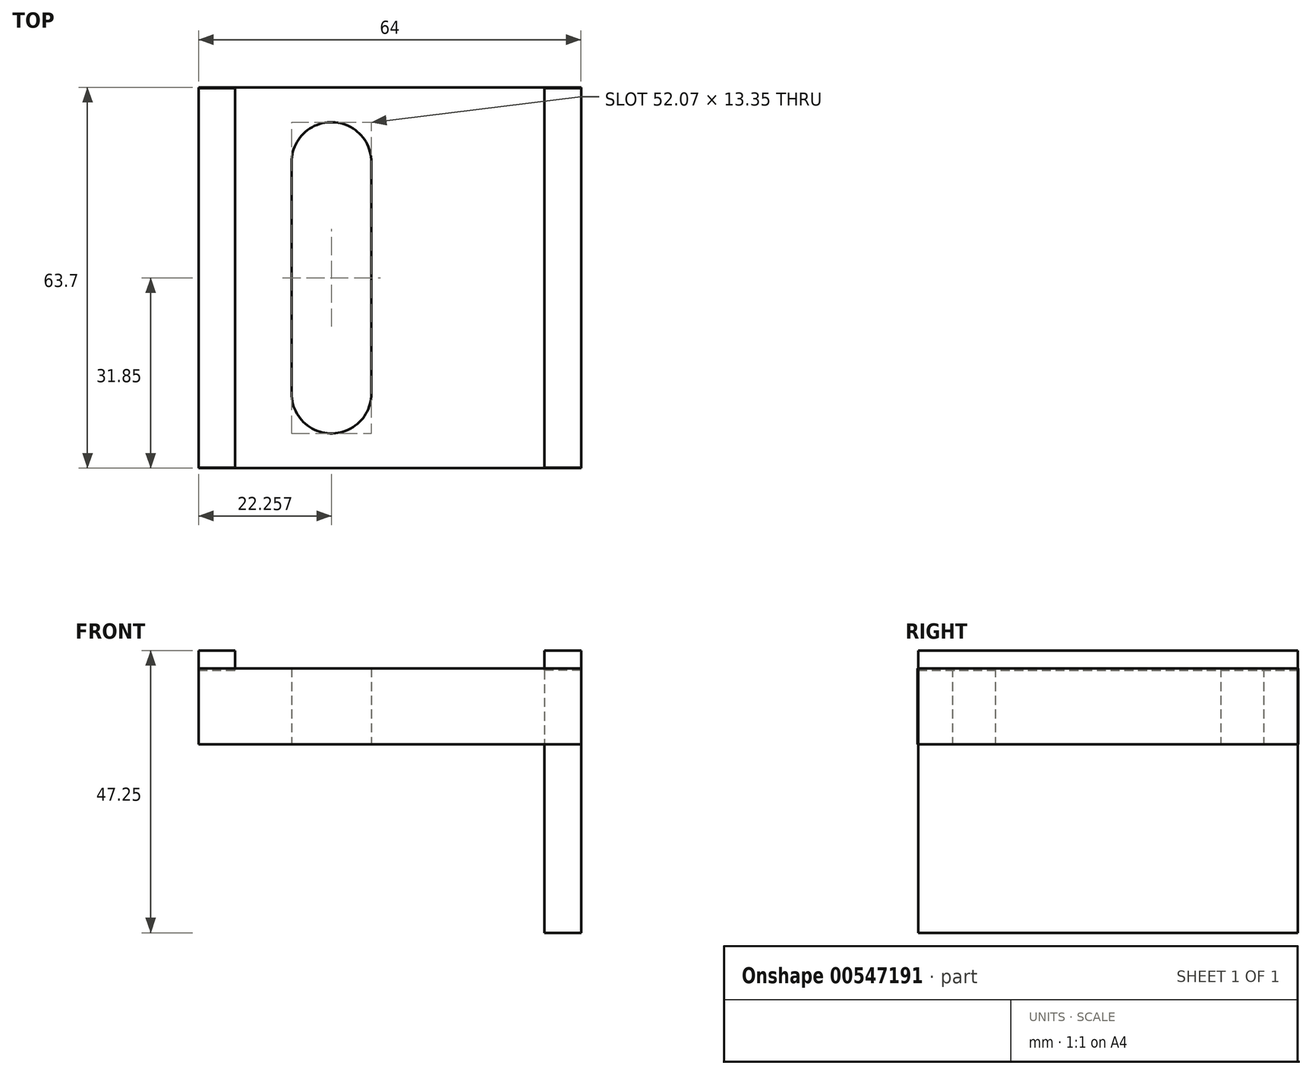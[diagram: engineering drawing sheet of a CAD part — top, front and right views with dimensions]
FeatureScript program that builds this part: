
annotation { "Feature Type Name" : "Feature", "Feature Type Description" : "" }
export const myFeature = defineFeature(function(context is Context, id is Id, definition is map)
    precondition{}
    {
        {
            var Q0;
            Q0=qCreatedBy(makeId("Top.planeOp"),FACE);
            var sketch = newSketch(context, id + "F0", { "sketchPlane" : qUnion([Q0])});
            skLineSegment(sketch, "E0.bottom", {"start": v(-32, 31.85) * mm, "end": v(32, 31.85) * mm});
            skLineSegment(sketch, "E0.top", {"start": v(-32, -31.85) * mm, "end": v(32, -31.85) * mm});
            skLineSegment(sketch, "E0.left", {"start": v(-32, 31.85) * mm, "end": v(-32, -31.85) * mm});
            skLineSegment(sketch, "E0.right", {"start": v(32, 31.85) * mm, "end": v(32, -31.85) * mm});
            skPoint(sketch, "E0.middle", {"position": v(0, 0) * mm});
            skLineSegment(sketch, "E1", {"start": v(-32, 31.85) * mm, "end": v(-9.75, 31.85) * mm});
            skLineSegment(sketch, "E2", {"start": v(-9.75, 31.85) * mm, "end": v(-9.75, 26.04) * mm});
            skArc(sketch, "E3", {"start": v(-3.07, 19.34) * mm, "mid": v(-9.99, 26.03) * mm, "end": v(-16.42, 18.87) * mm});
            skArc(sketch, "E4.MirrorC", {"start": v(-3.07, -19.35) * mm, "mid": v(-10, -26.03) * mm, "end": v(-16.42, -18.87) * mm});
            skLineSegment(sketch, "E5", {"start": v(-3.07, 19.37) * mm, "end": v(-3.07, -19.35) * mm});
            skLineSegment(sketch, "E6", {"start": v(-16.42, 19.84) * mm, "end": v(-16.42, -18.87) * mm});
            skLineSegment(sketch, "E7.trimOffspring", {"start": v(-9.75, -26.04) * mm, "end": v(-9.75, -31.85) * mm});
            skSolve(sketch);
        }
        {
            var Q0;
            {var subQ1=sQuery(id+"F0.wireOp",EDGE,"E0.left");Q0=makeQuery(id+"F0.imprint","IMPRINT",FACE,{"disambiguationData":[TD([[makeQuery(id+"F0.imprint","IMPRINT",EDGE,{"derivedFrom":subQ1}),1.0]])]});}
            var Q1;
            Q1=makeQuery(id+"F0.imprint","IMPRINT",FACE,{"disambiguationData":[TD([[makeQuery(id+"F0.imprint","IMPRINT",EDGE,{"derivedFrom":sQuery(id+"F0.wireOp",EDGE,"E0.bottom")}),-1.0]])]});
            extrude(context, id + "F1", {"entities" : qUnion([Q0, Q1]), "depth" : 12.7 * mm, "offsetDistance" : 25.4 * mm});
        }
        {
            var Q0;
            Q0=qCreatedBy(makeId("Front.planeOp"),FACE);
            var sketch = newSketch(context, id + "F2", { "sketchPlane" : qUnion([Q0])});
            skLineSegment(sketch, "E8.bottom", {"start": v(32, 12.34) * mm, "end": v(25.9, 12.34) * mm});
            skLineSegment(sketch, "E8.top", {"start": v(32, 15.7) * mm, "end": v(25.9, 15.7) * mm});
            skLineSegment(sketch, "E8.left", {"start": v(32, 12.34) * mm, "end": v(32, 15.7) * mm});
            skLineSegment(sketch, "E8.right", {"start": v(25.9, 12.34) * mm, "end": v(25.9, 15.7) * mm});
            skLineSegment(sketch, "E9.MirrorCS", {"start": v(-32, 12.34) * mm, "end": v(-25.9, 12.34) * mm});
            skLineSegment(sketch, "E10.MirrorCS", {"start": v(-32, 15.7) * mm, "end": v(-25.9, 15.7) * mm});
            skLineSegment(sketch, "E11", {"start": v(-25.9, 12.34) * mm, "end": v(-25.9, 15.7) * mm});
            skLineSegment(sketch, "E12", {"start": v(-32, 12.34) * mm, "end": v(-32, 15.7) * mm});
            skLineSegment(sketch, "E13", {"start": v(32, 12.34) * mm, "end": v(32, -31.55) * mm});
            skLineSegment(sketch, "E14", {"start": v(25.9, 12.34) * mm, "end": v(25.9, -31.55) * mm});
            skLineSegment(sketch, "E15", {"start": v(25.9, -31.55) * mm, "end": v(32, -31.55) * mm});
            skSolve(sketch);
        }
        {
            var Q0;
            Q0=makeQuery(id+"F2.imprint","IMPRINT",FACE,{"disambiguationData":[TD([[makeQuery(id+"F2.imprint","IMPRINT",EDGE,{"derivedFrom":sQuery(id+"F2.wireOp",EDGE,"E8.bottom")}),-1.0]])]});
            extrude(context, id + "F3", {"entities" : qUnion([Q0]), "depth" : 31.75 * mm, "offsetDistance" : 25.4 * mm, "hasSecondDirection" : true, "secondDirectionOppositeDirection" : true, "secondDirectionDepth" : 31.75 * mm});
        }
        {
            var Q0;
            Q0=makeQuery(id+"F2.imprint","IMPRINT",FACE,{"disambiguationData":[TD([[makeQuery(id+"F2.imprint","IMPRINT",EDGE,{"derivedFrom":sQuery(id+"F2.wireOp",EDGE,"E9.MirrorCS")}),1.0]])]});
            extrude(context, id + "F4", {"entities" : qUnion([Q0]), "depth" : 31.75 * mm, "offsetDistance" : 25.4 * mm, "hasSecondDirection" : true, "secondDirectionOppositeDirection" : true, "secondDirectionDepth" : 31.75 * mm});
        }
        {
            var Q0;
            Q0=makeQuery(id+"F2.imprint","IMPRINT",FACE,{"disambiguationData":[TD([[makeQuery(id+"F2.imprint","IMPRINT",EDGE,{"derivedFrom":sQuery(id+"F2.wireOp",EDGE,"E8.bottom")}),1.0]])]});
            extrude(context, id + "F5", {"entities" : qUnion([Q0]), "depth" : 31.75 * mm, "offsetDistance" : 25.4 * mm, "hasSecondDirection" : true, "secondDirectionOppositeDirection" : true, "secondDirectionDepth" : 31.75 * mm});
        }
    });
